# Revit family: Handshower-American_Standard-1660.637_Series
name_source: partatom
category: Plumbing Fixtures
revit_build: Autodesk Revit 2018 (Build: 20170223_1515(x64)
units: mm (PartAtom-declared; Revit-internal decimal feet)

## family parameters
Always vertical = No
Cut with Voids When Loaded = No
OmniClass Number = 23.45.05.14.17
OmniClass Title = Showers
Part Type = Normal
Room Calculation Point = No
Round Connector Dimension = Use Diameter
Shared = Yes
Work Plane-Based = Yes

## types (2) — shared parameters
Assembly Code = D2010710
CW Connection = No
CWFU = 3
Default Elevation = 0"
Description = Modern 5-Function Hand Shower
Face Diameter = 4 3/4"
Flow Rate = 2.5GPM (9.5LPM)
HW Connection = No
HWFU = 3
Height = 9 7/8"
IAPMO Compliance = ASME A112.18.1, CSA 125.1
Length = 3 3/4"
Manufacturer = American Standard
Price = Prices may vary. Please consult Manufacturer Representative for most up-to-date price list.
Product Documentation Link = https://www.americanstandard.ca
Product Page URL = https://www.americanstandard.ca
Revised Date = 09/28/2021
Tempered Water Connection = Yes
Tempered Water Connection Diameter = 1/2"
Tempered Water Connection Radius = 1/4"
URL = https://www.americanstandard.ca
Vent Connection = No
Warranty Information = 5 Year Limited Warranty
Warranty Information URL = https://www.americanstandard.ca
Waste Connection = No
Width = 3"
zero-valued in all types: WFU

## per-type parameters (varying)
| type | Finish | Material |
| 1660637.002 | Metal-American Standard-002-Polished Chrome | Metal-American Standard-002-Polished Chrome |
| 1660637.295 | Metal-American Standard-295-PVD Satin Nickel | Metal-American Standard-295-PVD Satin Nickel |

note: column(s) folded — value = type name in every type: Model

## geometry (parser evidence)
native form markers: Sweep x2
no freeform markers — native parametric forms only
